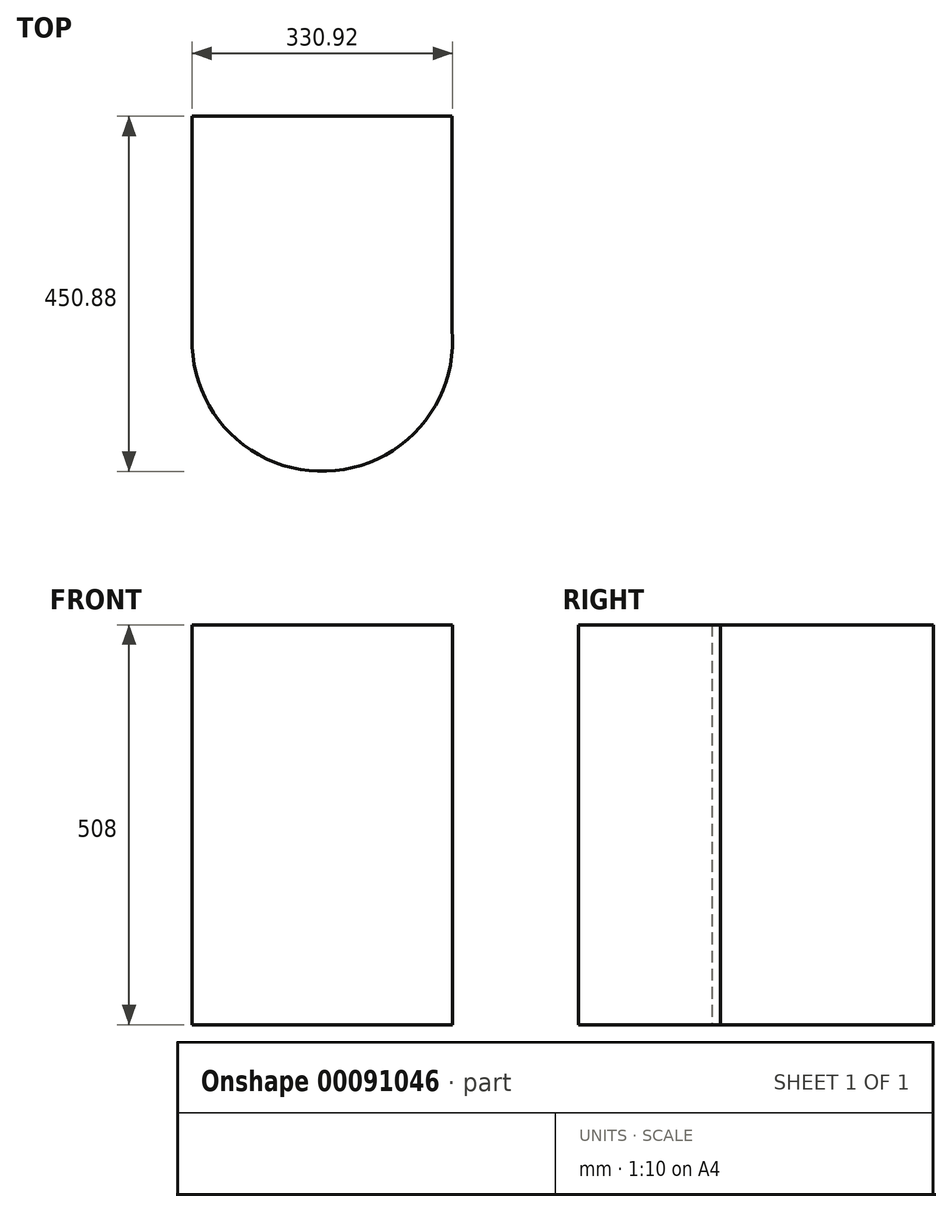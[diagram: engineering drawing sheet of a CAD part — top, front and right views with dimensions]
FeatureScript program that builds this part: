
annotation { "Feature Type Name" : "Feature", "Feature Type Description" : "" }
export const myFeature = defineFeature(function(context is Context, id is Id, definition is map)
    precondition{}
    {
        {
            var Q0;
            Q0=qCreatedBy(makeId("Top.planeOp"),FACE);
            var sketch = newSketch(context, id + "F0", { "sketchPlane" : qUnion([Q0])});
            skLineSegment(sketch, "E0.bottom", {"start": v(-162, 223.27) * mm, "end": v(168.2, 223.27) * mm});
            skLineSegment(sketch, "E0.top", {"start": v(0, -227.58) * mm, "end": v(6.84, -227.58) * mm});
            skLineSegment(sketch, "E0.left", {"start": v(-162, 223.27) * mm, "end": v(-162, -66.24) * mm});
            skLineSegment(sketch, "E0.right", {"start": v(168.2, 223.27) * mm, "end": v(168.2, -77) * mm});
            skArc(sketch, "E1", {"start": v(-162, -58.07) * mm, "mid": v(8.8, -227.53) * mm, "end": v(168.2, -47.31) * mm});
            skPoint(sketch, "E1.first.point", {"position": v(0, -227.58) * mm});
            skPoint(sketch, "E1.second.point", {"position": v(-162, -66.24) * mm});
            skPoint(sketch, "E1.third.point", {"position": v(168.2, -77) * mm});
            skSolve(sketch);
        }
        {
            var Q0;
            Q0 = qSketchRegion(id + "F0", true);
            extrude(context, id + "F1", {"entities" : qUnion([Q0]), "depth" : 508 * mm});
        }
    });
